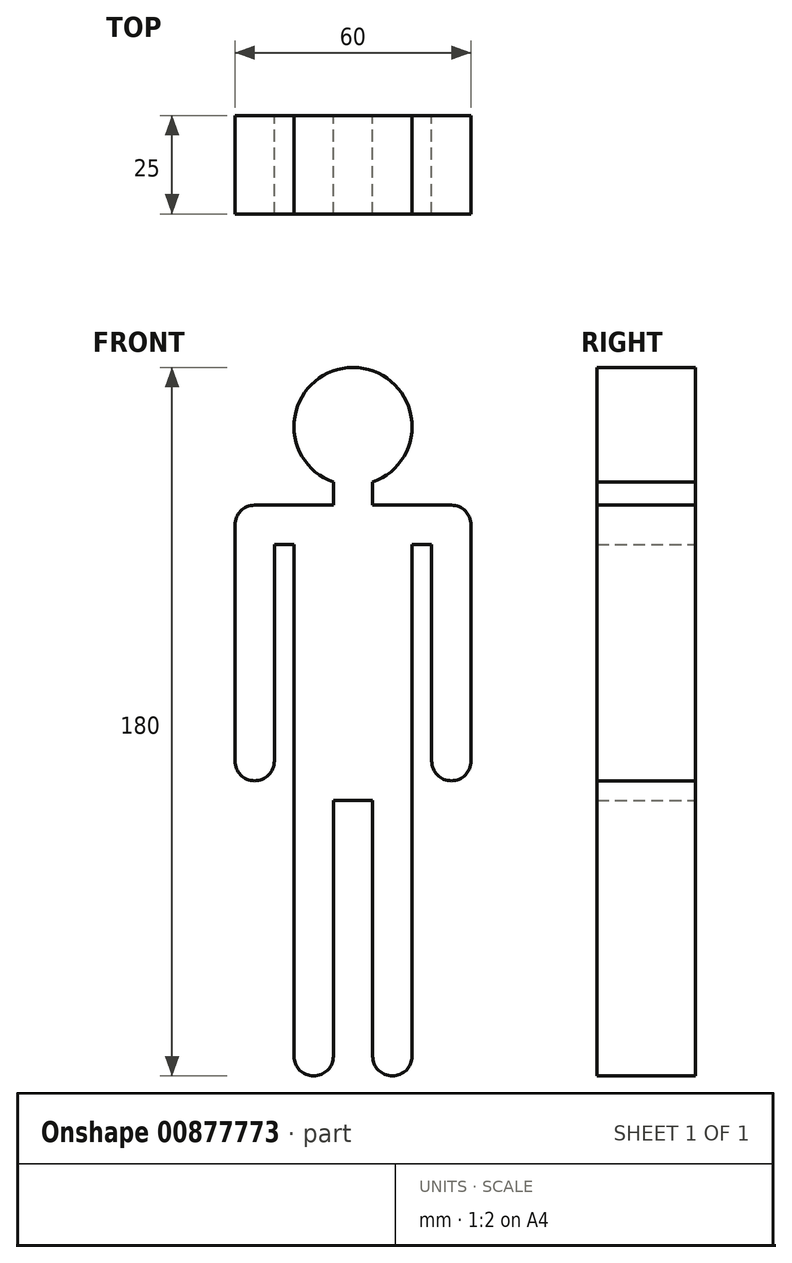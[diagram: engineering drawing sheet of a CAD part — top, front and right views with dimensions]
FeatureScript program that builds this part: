
annotation { "Feature Type Name" : "Feature", "Feature Type Description" : "" }
export const myFeature = defineFeature(function(context is Context, id is Id, definition is map)
    precondition{}
    {
        {
            var Q0;
            Q0=qCreatedBy(makeId("Front.planeOp"),FACE);
            var sketch = newSketch(context, id + "F0", { "sketchPlane" : qUnion([Q0])});
            skLineSegment(sketch, "E0.top", {"start": v(0, 180) * mm, "end": v(60, 180) * mm, "construction": true});
            skLineSegment(sketch, "E0.left", {"start": v(0, 0) * mm, "end": v(0, 180) * mm, "construction": true});
            skLineSegment(sketch, "E0.right", {"start": v(60, 0) * mm, "end": v(60, 180) * mm, "construction": true});
            skCircle(sketch, "E1", {"center": v(30, 165) * mm, "radius": 15 * mm});
            skPoint(sketch, "E1.centerSnap0", {"position": v(30, 180) * mm});
            skLineSegment(sketch, "E2", {"start": v(30, 165) * mm, "end": v(30, 140) * mm});
            skLineSegment(sketch, "E3", {"start": v(30, 140) * mm, "end": v(5, 140) * mm});
            skLineSegment(sketch, "E4", {"start": v(5, 140) * mm, "end": v(5, 80) * mm});
            skLineSegment(sketch, "E5", {"start": v(30, 140) * mm, "end": v(55, 140) * mm});
            skLineSegment(sketch, "E6", {"start": v(55, 140) * mm, "end": v(55, 80) * mm});
            skLineSegment(sketch, "E7", {"start": v(30, 140) * mm, "end": v(30, 75) * mm});
            skLineSegment(sketch, "E8", {"start": v(30, 75) * mm, "end": v(20, 75) * mm});
            skLineSegment(sketch, "E9", {"start": v(20, 75) * mm, "end": v(30, 75) * mm});
            skLineSegment(sketch, "E10", {"start": v(30, 75) * mm, "end": v(40, 75) * mm});
            skLineSegment(sketch, "E11", {"start": v(20, 75) * mm, "end": v(20, 5) * mm});
            skLineSegment(sketch, "E12", {"start": v(40, 75) * mm, "end": v(40, 5) * mm});
            skArc(sketch, "E13.0.startCap", {"start": v(0, 140) * mm, "mid": v(5, 145) * mm, "end": v(10, 140) * mm});
            skArc(sketch, "E13.0.endCap", {"start": v(10, 80) * mm, "mid": v(5, 75) * mm, "end": v(0, 80) * mm});
            skLineSegment(sketch, "E13.0.left", {"start": v(10, 140) * mm, "end": v(10, 80) * mm});
            skLineSegment(sketch, "E13.0.right", {"start": v(0, 140) * mm, "end": v(0, 80) * mm});
            skArc(sketch, "E13.1.startCap", {"start": v(30, 145) * mm, "mid": v(35, 140) * mm, "end": v(30, 135) * mm});
            skArc(sketch, "E13.1.endCap", {"start": v(5, 135) * mm, "mid": v(0, 140) * mm, "end": v(5, 145) * mm});
            skLineSegment(sketch, "E13.1.left", {"start": v(30, 135) * mm, "end": v(5, 135) * mm});
            skLineSegment(sketch, "E13.1.right", {"start": v(30, 145) * mm, "end": v(5, 145) * mm});
            skArc(sketch, "E13.2.startCap", {"start": v(30, 135) * mm, "mid": v(25, 140) * mm, "end": v(30, 145) * mm});
            skArc(sketch, "E13.2.endCap", {"start": v(55, 145) * mm, "mid": v(60, 140) * mm, "end": v(55, 135) * mm});
            skLineSegment(sketch, "E13.2.left", {"start": v(30, 145) * mm, "end": v(55, 145) * mm});
            skLineSegment(sketch, "E13.2.right", {"start": v(30, 135) * mm, "end": v(55, 135) * mm});
            skArc(sketch, "E13.3.startCap", {"start": v(50, 140) * mm, "mid": v(55, 145) * mm, "end": v(60, 140) * mm});
            skArc(sketch, "E13.3.endCap", {"start": v(60, 80) * mm, "mid": v(55, 75) * mm, "end": v(50, 80) * mm});
            skLineSegment(sketch, "E13.3.left", {"start": v(60, 140) * mm, "end": v(60, 80) * mm});
            skLineSegment(sketch, "E13.3.right", {"start": v(50, 140) * mm, "end": v(50, 80) * mm});
            skArc(sketch, "E13.4.startCap", {"start": v(35, 75) * mm, "mid": v(40, 80) * mm, "end": v(45, 75) * mm});
            skArc(sketch, "E13.4.endCap", {"start": v(45, 5) * mm, "mid": v(40, 0) * mm, "end": v(35, 5) * mm});
            skLineSegment(sketch, "E13.4.left", {"start": v(45, 75) * mm, "end": v(45, 5) * mm});
            skLineSegment(sketch, "E13.4.right", {"start": v(35, 75) * mm, "end": v(35, 5) * mm});
            skArc(sketch, "E13.5.startCap", {"start": v(15, 75) * mm, "mid": v(20, 80) * mm, "end": v(25, 75) * mm});
            skArc(sketch, "E13.5.endCap", {"start": v(25, 5) * mm, "mid": v(20, 0) * mm, "end": v(15, 5) * mm});
            skLineSegment(sketch, "E13.5.left", {"start": v(25, 75) * mm, "end": v(25, 5) * mm});
            skLineSegment(sketch, "E13.5.right", {"start": v(15, 75) * mm, "end": v(15, 5) * mm});
            skLineSegment(sketch, "E14", {"start": v(0, 0) * mm, "end": v(60, 0) * mm, "construction": true});
            skLineSegment(sketch, "E15", {"start": v(15, 75) * mm, "end": v(15, 135) * mm});
            skLineSegment(sketch, "E16", {"start": v(45, 75) * mm, "end": v(45, 135) * mm});
            skLineSegment(sketch, "E17", {"start": v(25, 70) * mm, "end": v(30, 70) * mm});
            skLineSegment(sketch, "E18", {"start": v(30, 75) * mm, "end": v(30, 70) * mm, "construction": true});
            skLineSegment(sketch, "E19", {"start": v(30, 70) * mm, "end": v(35, 70) * mm});
            skLineSegment(sketch, "E20", {"start": v(30, 150) * mm, "end": v(30, 145) * mm, "construction": true});
            skLineSegment(sketch, "E21", {"start": v(25, 140) * mm, "end": v(25, 150.86) * mm});
            skLineSegment(sketch, "E22", {"start": v(35, 140) * mm, "end": v(35, 150.86) * mm});
            skLineSegment(sketch, "E23", {"start": v(5, 140) * mm, "end": v(-55, 140) * mm, "construction": true});
            skLineSegment(sketch, "E24", {"start": v(55, 140) * mm, "end": v(115, 140) * mm, "construction": true});
            skLineSegment(sketch, "E25", {"start": v(5, 140) * mm, "end": v(5, 145) * mm, "construction": true});
            skCircle(sketch, "E26", {"center": v(-55, 140) * mm, "radius": 5 * mm, "construction": true});
            skCircle(sketch, "E27", {"center": v(115, 140) * mm, "radius": 5 * mm, "construction": true});
            skSolve(sketch);
        }
        {
            var Q0;
            Q0 = qSketchRegion(id + "F0", true);
            var Q1;
            {var subQ0=sQuery(id+"F0.wireOp",EDGE,"E5");var subQ3=sQuery(id+"F0.wireOp",EDGE,"E13.1.startCap");var subQ5=makeQuery(id+"F0.imprint","INTERSECT",VERTEX,{"derivedFrom":[subQ0,subQ3,sQuery(id+"F0.wireOp",EDGE,"E22")]});Q1=makeQuery(id+"F0.imprint","IMPRINT",FACE,{"disambiguationData":[TD([[makeQuery(id+"F0.imprint","IMPRINT",EDGE,{"disambiguationData":[TD([[subQ5,1.0]])],"derivedFrom":subQ0}),1.0]])]});}
            var Q2;
            {var subQ0=sQuery(id+"F0.wireOp",EDGE,"E3");var subQ3=sQuery(id+"F0.wireOp",EDGE,"E13.2.startCap");var subQ5=makeQuery(id+"F0.imprint","INTERSECT",VERTEX,{"derivedFrom":[subQ0,subQ3,sQuery(id+"F0.wireOp",EDGE,"E21")]});Q2=makeQuery(id+"F0.imprint","IMPRINT",FACE,{"disambiguationData":[TD([[makeQuery(id+"F0.imprint","IMPRINT",EDGE,{"disambiguationData":[TD([[subQ5,1.0]])],"derivedFrom":subQ0}),-1.0]])]});}
            var Q3;
            {var subQ1=sQuery(id+"F0.wireOp",EDGE,"E3");var subQ3=sQuery(id+"F0.wireOp",EDGE,"E13.2.startCap");var subQ4=makeQuery(id+"F0.imprint","INTERSECT",VERTEX,{"derivedFrom":[subQ1,subQ3,sQuery(id+"F0.wireOp",EDGE,"E21")]});Q3=makeQuery(id+"F0.imprint","IMPRINT",FACE,{"disambiguationData":[TD([[makeQuery(id+"F0.imprint","IMPRINT",EDGE,{"disambiguationData":[TD([[subQ4,1.0]])],"derivedFrom":subQ1}),1.0]])]});}
            var Q4;
            {var subQ1=sQuery(id+"F0.wireOp",EDGE,"E5");var subQ3=sQuery(id+"F0.wireOp",EDGE,"E13.1.startCap");var subQ4=makeQuery(id+"F0.imprint","INTERSECT",VERTEX,{"derivedFrom":[subQ1,subQ3,sQuery(id+"F0.wireOp",EDGE,"E22")]});Q4=makeQuery(id+"F0.imprint","IMPRINT",FACE,{"disambiguationData":[TD([[makeQuery(id+"F0.imprint","IMPRINT",EDGE,{"disambiguationData":[TD([[subQ4,1.0]])],"derivedFrom":subQ1}),-1.0]])]});}
            extrude(context, id + "F1", {"entities" : qUnion([Q0, Q1, Q2, Q3, Q4]), "depth" : 25 * mm, "offsetDistance" : 25 * mm});
        }
    });
